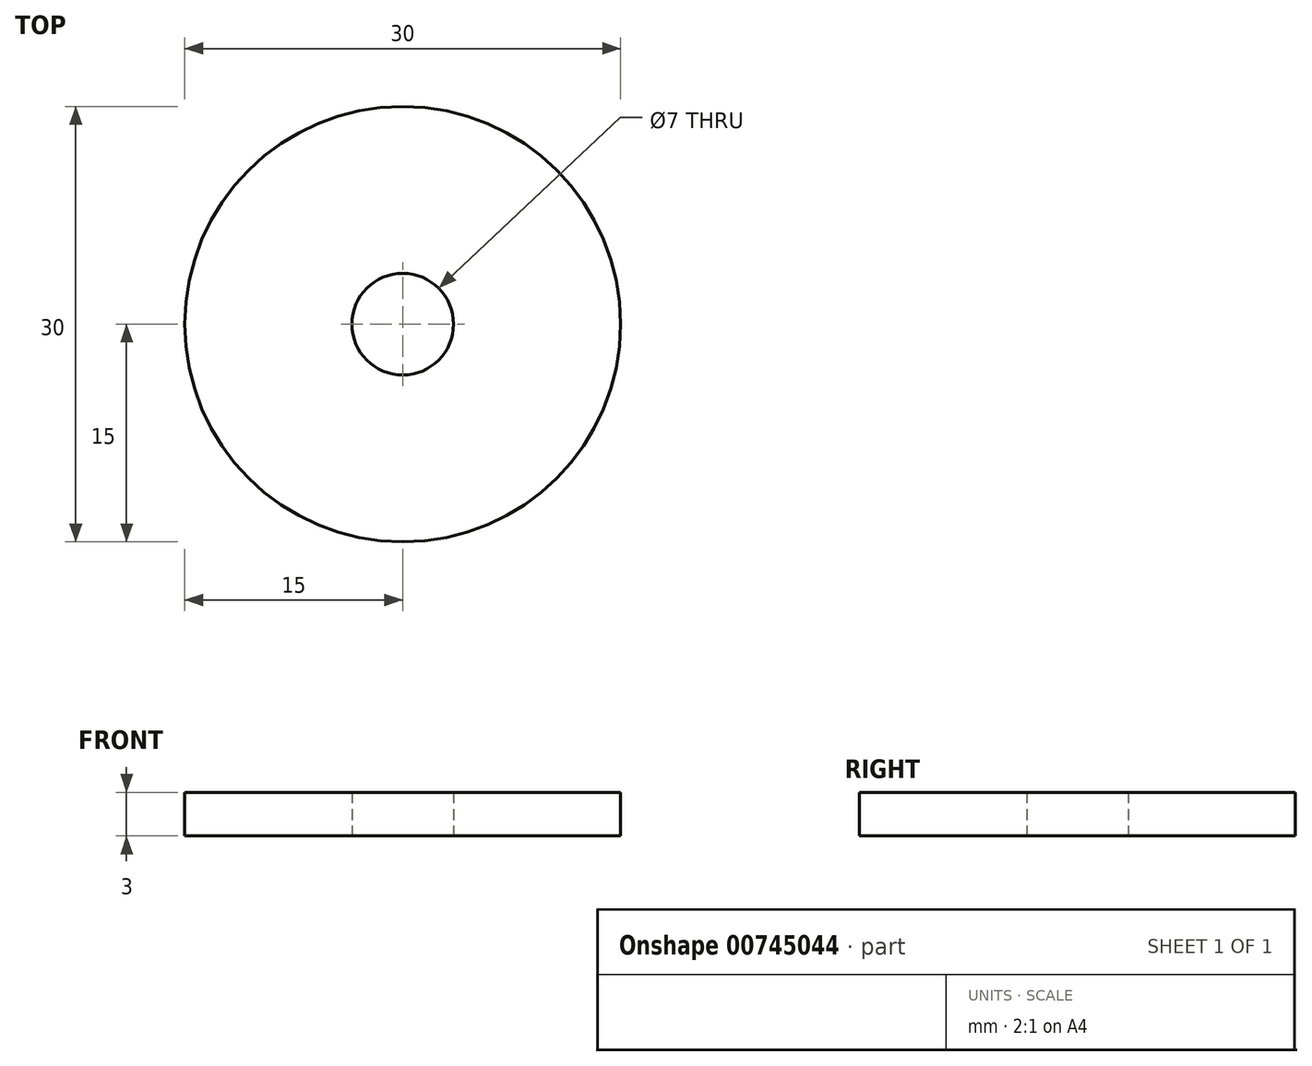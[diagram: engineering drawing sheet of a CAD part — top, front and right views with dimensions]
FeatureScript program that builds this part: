
annotation { "Feature Type Name" : "Feature", "Feature Type Description" : "" }
export const myFeature = defineFeature(function(context is Context, id is Id, definition is map)
    precondition{}
    {
        {
            var Q0;
            Q0=qCreatedBy(makeId("Top.planeOp"),FACE);
            var sketch = newSketch(context, id + "F0", { "sketchPlane" : qUnion([Q0])});
            skCircle(sketch, "E0", {"center": v(0, 0) * mm, "radius": 15 * mm});
            skCircle(sketch, "E1", {"center": v(0, 0) * mm, "radius": 3.5 * mm});
            skSolve(sketch);
        }
        {
            var Q0;
            Q0 = qSketchRegion(id + "F0", true);
            extrude(context, id + "F1", {"entities" : qUnion([Q0]), "depth" : 3 * mm, "offsetDistance" : 25 * mm});
        }
    });
